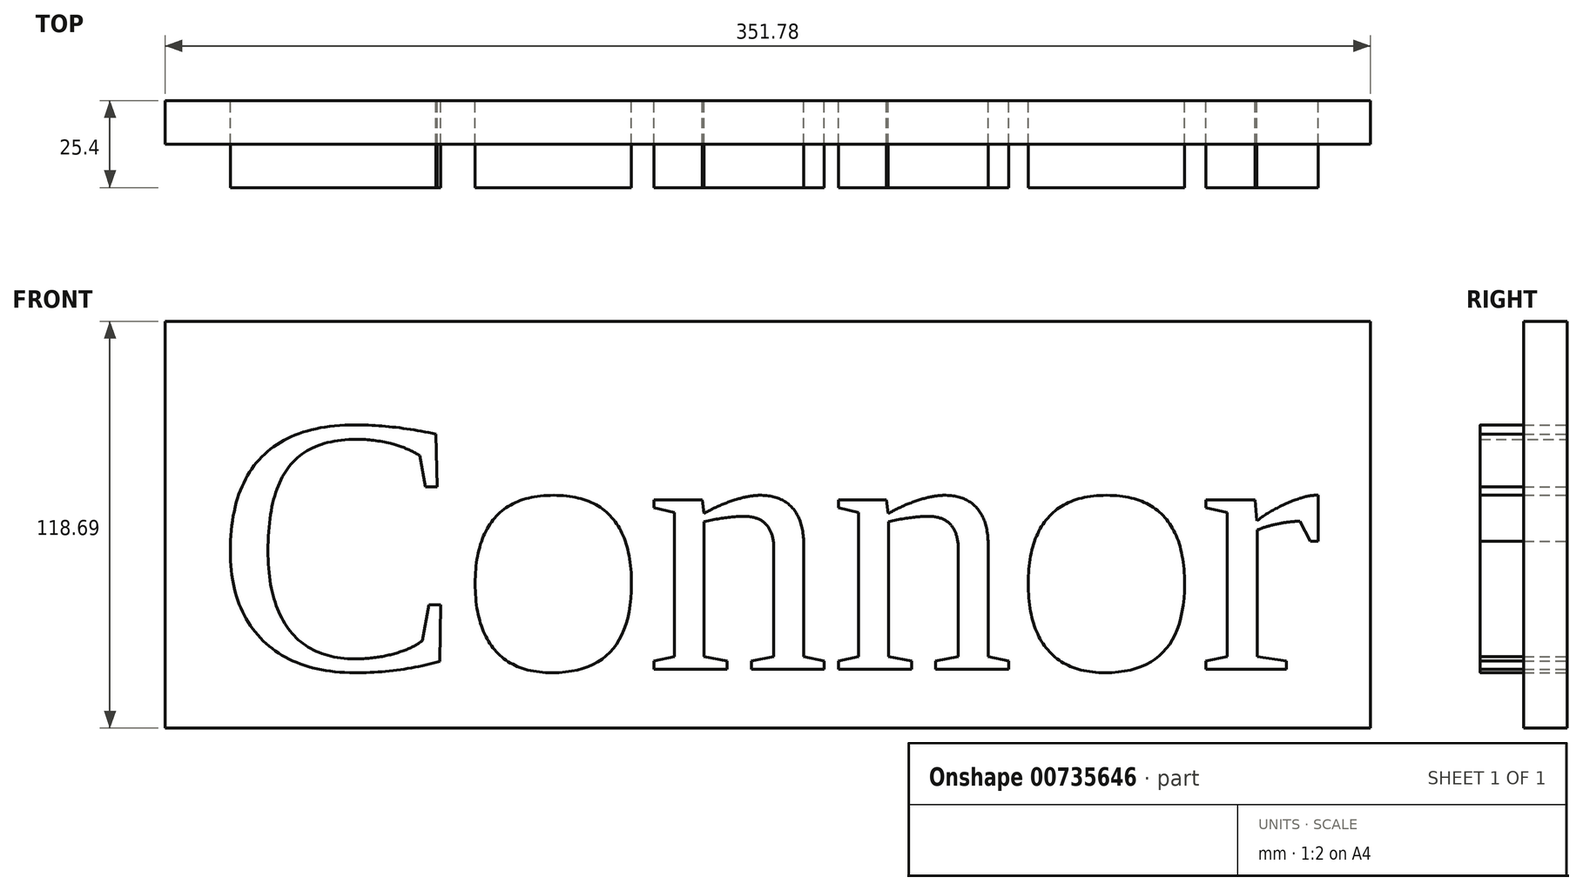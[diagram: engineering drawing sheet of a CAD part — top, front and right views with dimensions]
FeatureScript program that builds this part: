
annotation { "Feature Type Name" : "Feature", "Feature Type Description" : "" }
export const myFeature = defineFeature(function(context is Context, id is Id, definition is map)
    precondition{}
    {
        {
            var Q0;
            Q0=qCreatedBy(makeId("Front.planeOp"),FACE);
            var sketch = newSketch(context, id + "F0", { "sketchPlane" : qUnion([Q0])});
            skText(sketch, "E0", { "text": "Connor\n", "fontName": "Tinos-Regular.ttf"});
            skLineSegment(sketch, "E1.bottom", {"start": v(-198.59, 64.1) * mm, "end": v(191.29, 64.1) * mm});
            skLineSegment(sketch, "E1.top", {"start": v(-198.59, -62.77) * mm, "end": v(191.29, -62.77) * mm});
            skLineSegment(sketch, "E1.left", {"start": v(-198.59, 64.1) * mm, "end": v(-198.59, -62.77) * mm});
            skLineSegment(sketch, "E1.right", {"start": v(191.29, 64.1) * mm, "end": v(191.29, -62.77) * mm});
            const initialGuessF0  = {"E0": [-0.185, -0.03225, 1, 0, 0.07746]};
            skSetInitialGuess(sketch, initialGuessF0);
            skSolve(sketch);
        }
        {
            var Q0;
            Q0=makeQuery(id+"F0.imprint","IMPRINT",FACE,{"disambiguationData":[TD([[makeQuery(id+"F0.imprint","IMPRINT",EDGE,{"derivedFrom":sQuery(id+"F0.wireOp",EDGE,"E0.sketch_text.stroke-20")}),-1.0]])]});
            var Q1;
            Q1=makeQuery(id+"F0.imprint","IMPRINT",FACE,{"disambiguationData":[TD([[makeQuery(id+"F0.imprint","IMPRINT",EDGE,{"derivedFrom":sQuery(id+"F0.wireOp",EDGE,"E0.sketch_text.stroke-0")}),-1.0]])]});
            var Q2;
            Q2=makeQuery(id+"F0.imprint","IMPRINT",FACE,{"disambiguationData":[TD([[makeQuery(id+"F0.imprint","IMPRINT",EDGE,{"derivedFrom":sQuery(id+"F0.wireOp",EDGE,"E0.sketch_text.stroke-27")}),1.0]])]});
            var Q3;
            Q3=makeQuery(id+"F0.imprint","IMPRINT",FACE,{"disambiguationData":[TD([[makeQuery(id+"F0.imprint","IMPRINT",EDGE,{"derivedFrom":sQuery(id+"F0.wireOp",EDGE,"E0.sketch_text.stroke-35")}),-1.0]])]});
            var Q4;
            Q4=makeQuery(id+"F0.imprint","IMPRINT",FACE,{"disambiguationData":[TD([[makeQuery(id+"F0.imprint","IMPRINT",EDGE,{"derivedFrom":sQuery(id+"F0.wireOp",EDGE,"E0.sketch_text.stroke-85")}),-1.0]])]});
            var Q5;
            Q5=makeQuery(id+"F0.imprint","IMPRINT",FACE,{"disambiguationData":[TD([[makeQuery(id+"F0.imprint","IMPRINT",EDGE,{"derivedFrom":sQuery(id+"F0.wireOp",EDGE,"E0.sketch_text.stroke-92")}),1.0]])]});
            var Q6;
            Q6=makeQuery(id+"F0.imprint","IMPRINT",FACE,{"disambiguationData":[TD([[makeQuery(id+"F0.imprint","IMPRINT",EDGE,{"derivedFrom":sQuery(id+"F0.wireOp",EDGE,"E0.sketch_text.stroke-100")}),-1.0]])]});
            var Q7;
            Q7=makeQuery(id+"F0.imprint","IMPRINT",FACE,{"disambiguationData":[TD([[makeQuery(id+"F0.imprint","IMPRINT",EDGE,{"derivedFrom":sQuery(id+"F0.wireOp",EDGE,"E0.sketch_text.stroke-60")}),-1.0]])]});
            extrude(context, id + "F1", {"entities" : qUnion([Q0, Q1, Q2, Q3, Q4, Q5, Q6, Q7]), "depth" : 25.4 * mm, "offsetDistance" : 25.4 * mm});
        }
        {
            var Q0;
            Q0=qCreatedBy(makeId("Front.planeOp"),FACE);
            var sketch = newSketch(context, id + "F2", { "sketchPlane" : qUnion([Q0])});
            skLineSegment(sketch, "E2.bottom", {"start": v(-199.66, 69.2) * mm, "end": v(152.12, 69.2) * mm});
            skLineSegment(sketch, "E2.top", {"start": v(-199.66, -49.5) * mm, "end": v(152.12, -49.5) * mm});
            skLineSegment(sketch, "E2.left", {"start": v(-199.66, 69.2) * mm, "end": v(-199.66, -49.5) * mm});
            skLineSegment(sketch, "E2.right", {"start": v(152.12, 69.2) * mm, "end": v(152.12, -49.5) * mm});
            skSolve(sketch);
        }
        {
            var Q0;
            Q0=makeQuery(id+"F2.imprint","IMPRINT",FACE,{"disambiguationData":[TD([[makeQuery(id+"F2.imprint","IMPRINT",EDGE,{"derivedFrom":sQuery(id+"F2.wireOp",EDGE,"E2.bottom")}),-1.0]])]});
            extrude(context, id + "F3", {"entities" : qUnion([Q0]), "depth" : 12.7 * mm, "offsetDistance" : 25.4 * mm});
        }
    });
